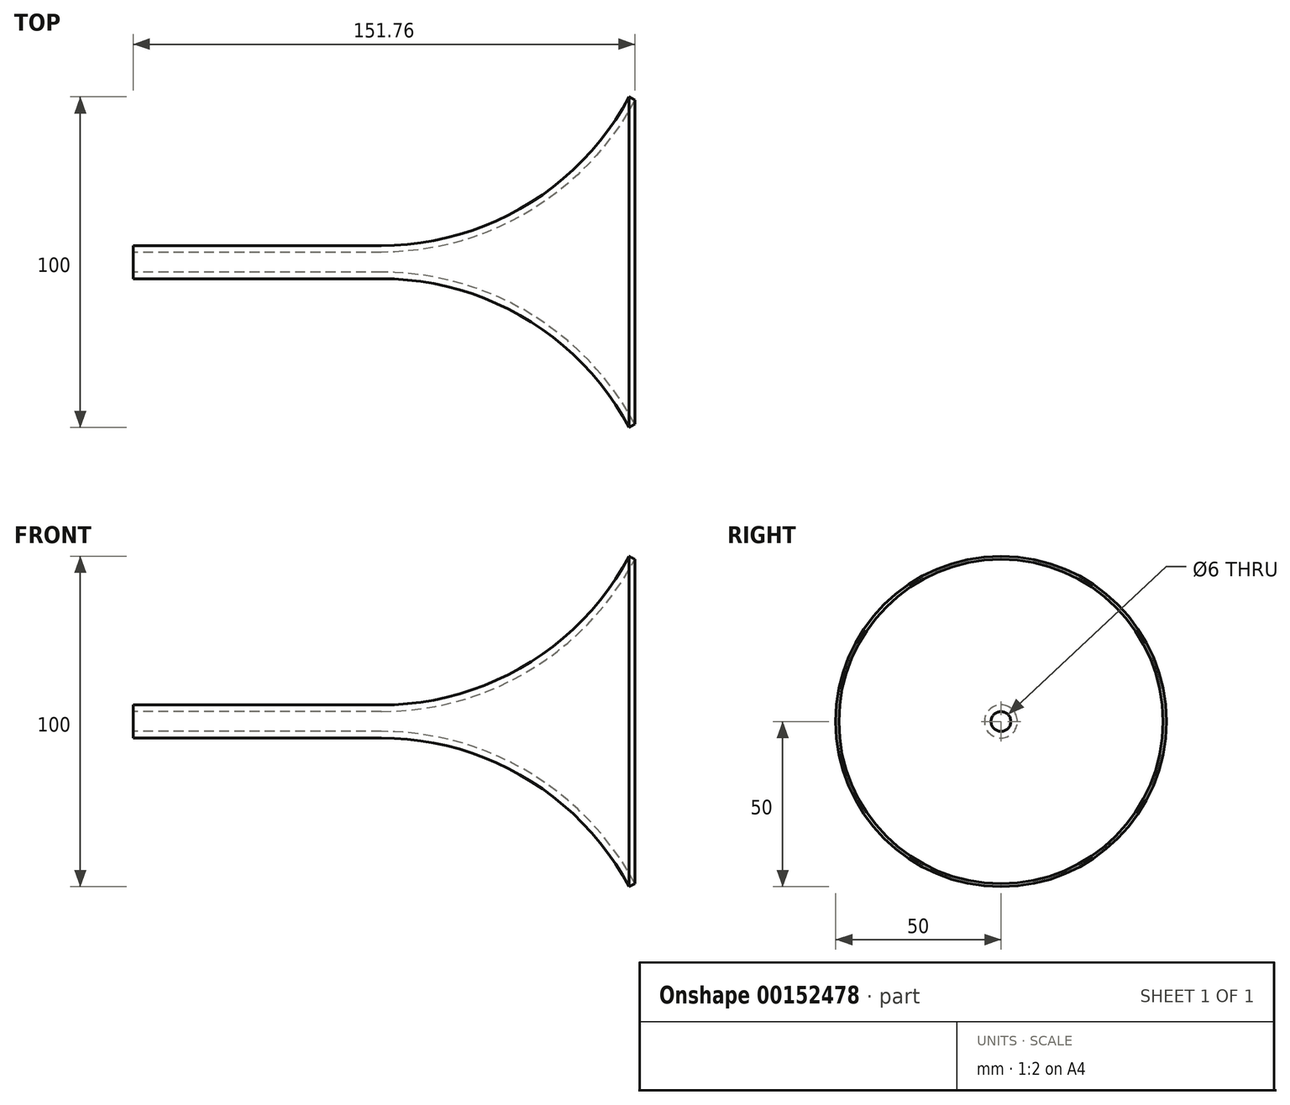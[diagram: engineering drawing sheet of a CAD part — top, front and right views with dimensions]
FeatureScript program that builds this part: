
annotation { "Feature Type Name" : "Feature", "Feature Type Description" : "" }
export const myFeature = defineFeature(function(context is Context, id is Id, definition is map)
    precondition{}
    {
        {
            var Q0;
            Q0=qCreatedBy(makeId("Front.planeOp"),FACE);
            var sketch = newSketch(context, id + "F0", { "sketchPlane" : qUnion([Q0])});
            skLineSegment(sketch, "E0", {"start": v(-53.69, 0) * mm, "end": v(69.12, 0) * mm, "construction": true});
            skLineSegment(sketch, "E1", {"start": v(-75, 5) * mm, "end": v(0, 5) * mm});
            skArc(sketch, "E2", {"start": v(0, 5) * mm, "mid": v(43.73, 17.11) * mm, "end": v(75, 50) * mm});
            skArc(sketch, "E3.0", {"start": v(0, 3) * mm, "mid": v(44.76, 15.4) * mm, "end": v(76.76, 49.06) * mm});
            skLineSegment(sketch, "E3.1", {"start": v(-75, 3) * mm, "end": v(0, 3) * mm});
            skLineSegment(sketch, "E4", {"start": v(75, 50) * mm, "end": v(76.76, 49.06) * mm});
            skLineSegment(sketch, "E5", {"start": v(-75, 5) * mm, "end": v(-75, 3) * mm});
            skPoint(sketch, "E6.end.orphan", {"position": v(75, 5.38) * mm});
            skSolve(sketch);
        }
        {
            var Q0;
            Q0=makeQuery(id+"F0.imprint","IMPRINT",FACE,{"disambiguationData":[TD([[makeQuery(id+"F0.imprint","IMPRINT",EDGE,{"derivedFrom":sQuery(id+"F0.wireOp",EDGE,"E1")}),-1.0]])]});
            var Q1;
            Q1=sQuery(id+"F0.wireOp",EDGE,"E0");
            revolve(context, id + "F1", {"entities" : qUnion([Q0]), "axis" : qUnion([Q1]), "revolveType" : RevolveType.FULL});
        }
    });
